annotation { "Feature Type Name" : "Feature", "Feature Type Description" : "" }
export const myFeature = defineFeature(function(context is Context, id is Id, definition is map)
    precondition{}
    {
        {
            var Q0;
            Q0=qCreatedBy(makeId("Top.planeOp"),FACE);
            var sketch = newSketch(context, id + "F0", { "sketchPlane" : qUnion([Q0])});
            skLineSegment(sketch, "E0.bottom", {"start": v(75, -35) * mm, "end": v(-75, -35) * mm});
            skLineSegment(sketch, "E0.top", {"start": v(75, 35) * mm, "end": v(-75, 35) * mm});
            skLineSegment(sketch, "E0.left", {"start": v(75, -35) * mm, "end": v(75, 35) * mm});
            skLineSegment(sketch, "E0.right", {"start": v(-75, -35) * mm, "end": v(-75, 35) * mm});
            skPoint(sketch, "E0.middle", {"position": v(0, 0) * mm});
            skSolve(sketch);
        }
        {
            var Q0;
            Q0=makeQuery(id+"F0.imprint","IMPRINT",FACE,{"disambiguationData":[TD([[makeQuery(id+"F0.imprint","IMPRINT",EDGE,{"derivedFrom":sQuery(id+"F0.wireOp",EDGE,"E0.bottom")}),-1.0]])]});
            extrude(context, id + "F1", {"entities" : qUnion([Q0]), "depth" : 100 * mm});
        }
        {
            var Q0;
            Q0=makeQuery(id+"F1.opExtrude","CAP_FACE",FACE,{"disambiguationData":[OSD([sQuery(id+"F0.wireOp",EDGE,"E0.bottom"),sQuery(id+"F0.wireOp",EDGE,"E0.top"),sQuery(id+"F0.wireOp",EDGE,"E0.left"),sQuery(id+"F0.wireOp",EDGE,"E0.right")])],"isStart":false});
            shell(context, id + "F2", {"entities" : qUnion([Q0]), "thickness" : 5 * mm});
        }
        {
            var Q0;
            Q0=makeQuery(id+"F1.opExtrude","SWEPT_FACE",FACE,{"disambiguationData":[OSD([sQuery(id+"F0.wireOp",EDGE,"E0.bottom")])]});
            var sketch = newSketch(context, id + "F3", { "sketchPlane" : qUnion([Q0])});
            skText(sketch, "E1", { "text": "Yoon Ji-Hoo", "fontName": "OpenSans-Regular.ttf"});
            skText(sketch, "E2", { "text": "Geum Jan-Di", "fontName": "OpenSans-Regular.ttf"});
            skText(sketch, "E3", { "text": "So Yi-Jung", "fontName": "OpenSans-Regular.ttf"});
            skText(sketch, "E4", { "text": "Song Woo-Bin", "fontName": "OpenSans-Regular.ttf"});
            skText(sketch, "E5", { "text": "Gu Jun-Pyo", "fontName": "OpenSans-Regular.ttf"});
            skLineSegment(sketch, "E6", {"start": v(-24.59, 87.87) * mm, "end": v(20.31, 87.87) * mm, "construction": true});
            skLineSegment(sketch, "E7", {"start": v(0, 0) * mm, "end": v(-0.02, 11.15) * mm, "construction": true});
            skLineSegment(sketch, "E8", {"start": v(-0.02, 11.15) * mm, "end": v(-27.3, 11.1) * mm, "construction": true});
            skLineSegment(sketch, "E9", {"start": v(-0.02, 11.15) * mm, "end": v(11.57, 11.15) * mm, "construction": true});
            skLineSegment(sketch, "E10", {"start": v(-0.1, 87.87) * mm, "end": v(-0.1, 58.05) * mm, "construction": true});
            skPoint(sketch, "E10.startSnap0", {"position": v(-2.14, 87.87) * mm});
            skLineSegment(sketch, "E11", {"start": v(-0.1, 87.87) * mm, "end": v(-0.1, 100) * mm, "construction": true});
            skLineSegment(sketch, "E12", {"start": v(-0.1, 43.05) * mm, "end": v(-0.02, 11.15) * mm, "construction": true});
            const initialGuessF3  = {"E1": [0.0219, 0.08087, 1, 0, 0.007], "E2": [-0.06072, 0.04305, 1, 0, 0.015], "E3": [-0.07494, 0.01103, 1, 0, 0.007], "E4": [0.01157, 0.01108, 1, 0, 0.007], "E5": [-0.07452, 0.08087, 1, 0, 0.007]};
            skSetInitialGuess(sketch, initialGuessF3);
            skSolve(sketch);
        }
        {
            var Q0;
            Q0=qConstructionFilter(qBodyType(qCreatedBy(id+"F3",EDGE),BodyType.WIRE),ConstructionObject.NO);
            extrude(context, id + "F4", {"bodyType" : ToolBodyType.SURFACE, "surfaceEntities" : qUnion([Q0]), "depth" : 5 * mm});
        }
    });